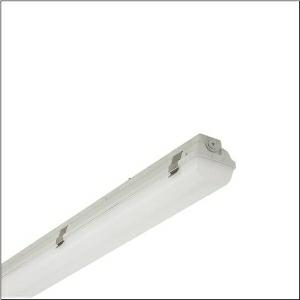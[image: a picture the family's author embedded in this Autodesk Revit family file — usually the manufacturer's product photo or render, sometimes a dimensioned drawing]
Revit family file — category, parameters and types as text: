
# Revit family: monsun_r__21_eco_51fj10ml45a_013e
name_source: partatom
category: Lighting Fixtures
units: mm (PartAtom-declared; Revit-internal decimal feet)

## family parameters
Cut with Voids When Loaded = No
Host = Face
Light Source = No
Part Type = Normal
Room Calculation Point = No
Round Connector Dimension = Use Diameter
Shared = No

## types (1)
- --- (1 x LED, 5000 lm, 36 W, 4000K)
    Apparent Load = 36 VA
    CIE Flux Codes = 41 70 89 90 100
    Color Rendering = 80
    Color Temperature = 4000K
    Default Elevation = 1800 mm
    Description = Monsun® 21 Eco, damp-proof luminaire, primary optical cover: diffuser, of PMMA, frosted, light emission: direct distribution, primary light characteristic: symmetric, installation type: suspended mounting, surface-mounted, LED, rated luminous flux: 5.000lm, luminous efficacy: 139lm/W, light colour: 840, colour temperature: 4000K, control gear: ECG Multilumen, with terminal, 3-pole, max. 2.5mm², mains connection: 220..240V, AC, 50/60Hz, rated input power: 36W, housing, of glass-fibre reinforced polyester, light grey (RAL 7035), length: 1.277mm, width: 90mm, height: 95mm, clip for enclosure, of spring steel V2A, protection rating (complete): IP66, insulation class (complete): insulation class I (protective earthing), certification: CE, UKCA, protection symbol: D, impact resistance: IK02, permissible operating ambient temperature: -20..+35°C, corresponds to IFS (International Featured Standards) requirements for safety and quality in the food industry, packaging unit: 1 piece
    Height = 103 mm
    Lamp = 1 x LED
    Lamp Light Flux = 5000 lm
    Lamp Power = 36 W
    Lamp count = 1
    Length = 1277 mm
    Luminous efficacy = 139 lm/W
    Manufacturer = Siteco
    ModVariant = No
    Model = 51FJ10ML45A
    Mounting Place = Ceiling
    Mounting Type = Surface mounted
    Number of Poles = 1
    OnlyDefault = Yes
    Power Factor = 1
    Product Name = Monsun® 21 Eco
    Product group = damp-proof luminaire | ceiling mounted
    ProductGroupID = 300
    Protection Class = Protection class I
    Protection Degree = IP 66
    RLX_Detail_Level = 1
    RlxData = <blob elided: 33829 chars, md5=12c3d0cc>
    Socket = socket
    Standby Power = 0 W
    System Light Flux = 5000 lm
    System Power = 36 W
    Type Comments = factory setting: luminous flux: 100 % | (ON | ON | ON | ON) | 350 mA
    Type Image = l_1007218.jpg
    URL = http://relux.com
    VarID = @adj_055477
    Voltage = 0 V
    Weight = 0.00 kg
    Width = 90 mm

## geometry (parser evidence)
native form markers: Blend x4, Sweep x13
no freeform markers — native parametric forms only
